# Revit family: Höhenversteller
name_source: partatom
category: HLS-Bauteile
revit_build: Autodesk Revit 2017 (Build: 20190507_1515(x64)
units: mm (PartAtom-declared; Revit-internal decimal feet)

## family parameters
Arbeitsebenenbasiert = Ja
Beim Laden mit Abzugskörper schneiden = Nein
Bemaßung runder Anschluss = Durchmesser verwenden
Gemeinsam genutzt = Ja
Immer vertikal = Nein
Raumberechnungspunkt = Nein
Teiletyp = Normal

## types (2) — shared parameters
Breite = 30 mm  [stored 0.0984252 ft]
Fabrikat = MEFA
Firma = MEFA Befestigungs- und Montagesysteme GmbH
Gewicht = 0.10 kg
Gewicht pro Bauteil = 0.10 kg
Gleitfunktion = nein
Höhe = 56 mm
Höhe verstellbar = 30 mm
Kurztext1 = Höhenversteller verst. H 30 mm
Länge = 31 mm  [stored 0.101706 ft]
Material = Stahl
Materialname = S235
Mengeneinheit = St
Oberflaeche = galvanisch verzinkt
Vorgabe-Ansicht = 1219 mm
max. zul. Last = 3.00 kN
vpe = 50 St
zero-valued in all types: Lochdurchmesser 1, Lochdurchmesser 2

## per-type parameters (varying)
| type | Artikelnummer | Bandbuchse | EAN | Gewindeplatte Vierkant | Kurztext2 | für Gewinde |
| Höhenversteller M 8/SMU8 | 0783021 | Bundbuchse M8 verdreht : Bandbuchse M8 | 4250928418722 | MEFA Gewindeplatte Vierkant : MEFA Gewindeplatte Vierkant 17x 17x 5 M 8 | für Gewinde M8 | M8 |
| Höhenversteller M10/SMU10 | 0783110 | Bundbuchse M8 verdreht : Bandbuchse M10 | 4250928418739 | MEFA Gewindeplatte Vierkant : MEFA Gewindeplatte Vierkant 17x 17x 5 M10 | für Gewinde M10 | M10 |

note: [stored X ft] marks values corroborated as IEEE doubles in the binary element streams (Revit-internal decimal feet)
